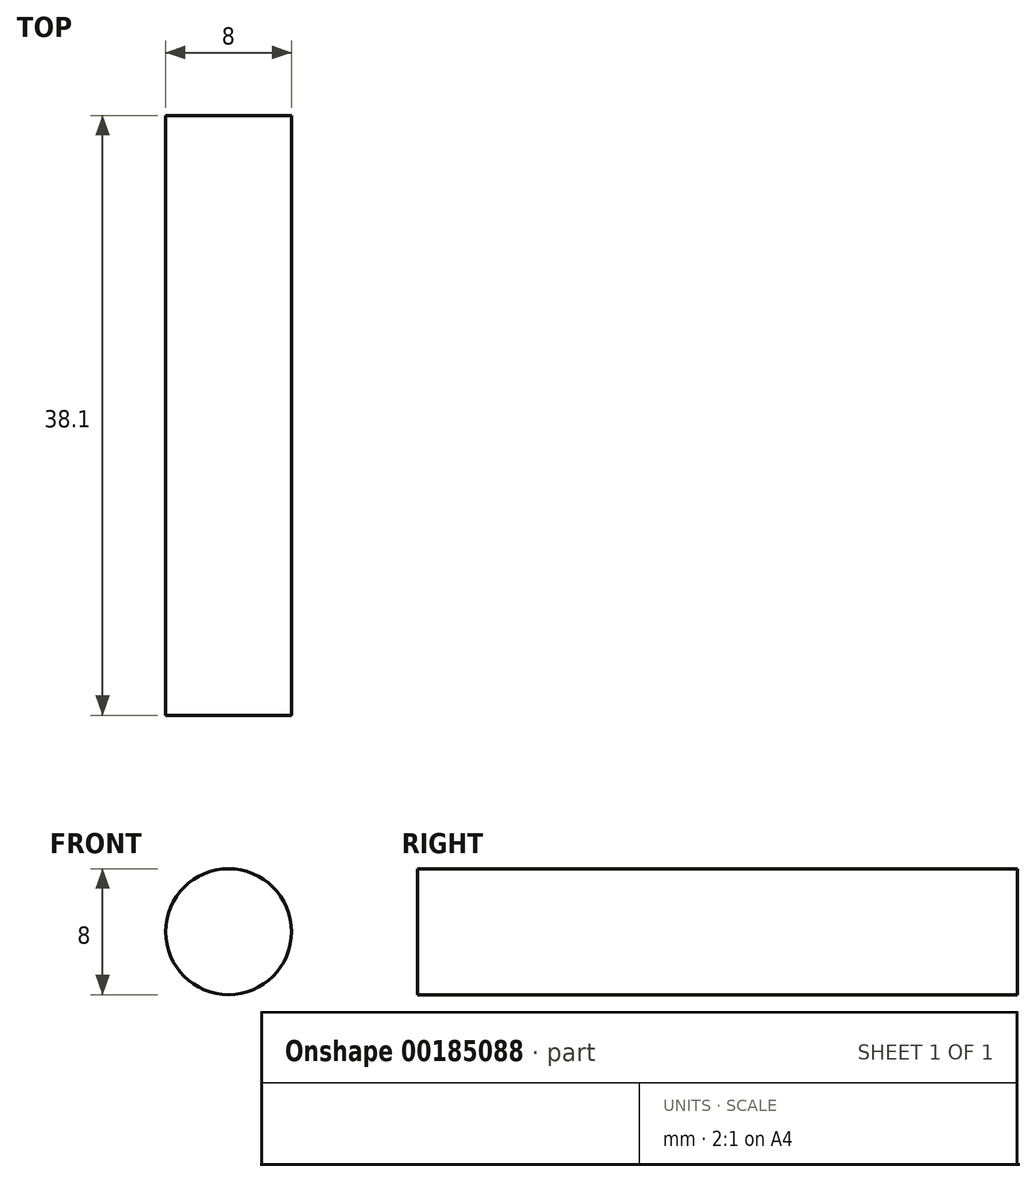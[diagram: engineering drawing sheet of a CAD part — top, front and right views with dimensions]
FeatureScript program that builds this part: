
annotation { "Feature Type Name" : "Feature", "Feature Type Description" : "" }
export const myFeature = defineFeature(function(context is Context, id is Id, definition is map)
    precondition{}
    {
        {
            var Q0;
            Q0=qCreatedBy(makeId("Front.planeOp"),FACE);
            var sketch = newSketch(context, id + "F0", { "sketchPlane" : qUnion([Q0])});
            skCircle(sketch, "E0", {"center": v(0, 0) * mm, "radius": 4 * mm});
            skSolve(sketch);
        }
        {
            var Q0;
            Q0=makeQuery(id+"F0.imprint","IMPRINT",FACE,{"disambiguationData":[TD([[makeQuery(id+"F0.imprint","IMPRINT",EDGE,{"derivedFrom":sQuery(id+"F0.wireOp",EDGE,"E0")}),1.0]])]});
            extrude(context, id + "F1", {"entities" : qUnion([Q0]), "endBound" : BoundingType.SYMMETRIC, "depth" : 38.1 * mm});
        }
    });
